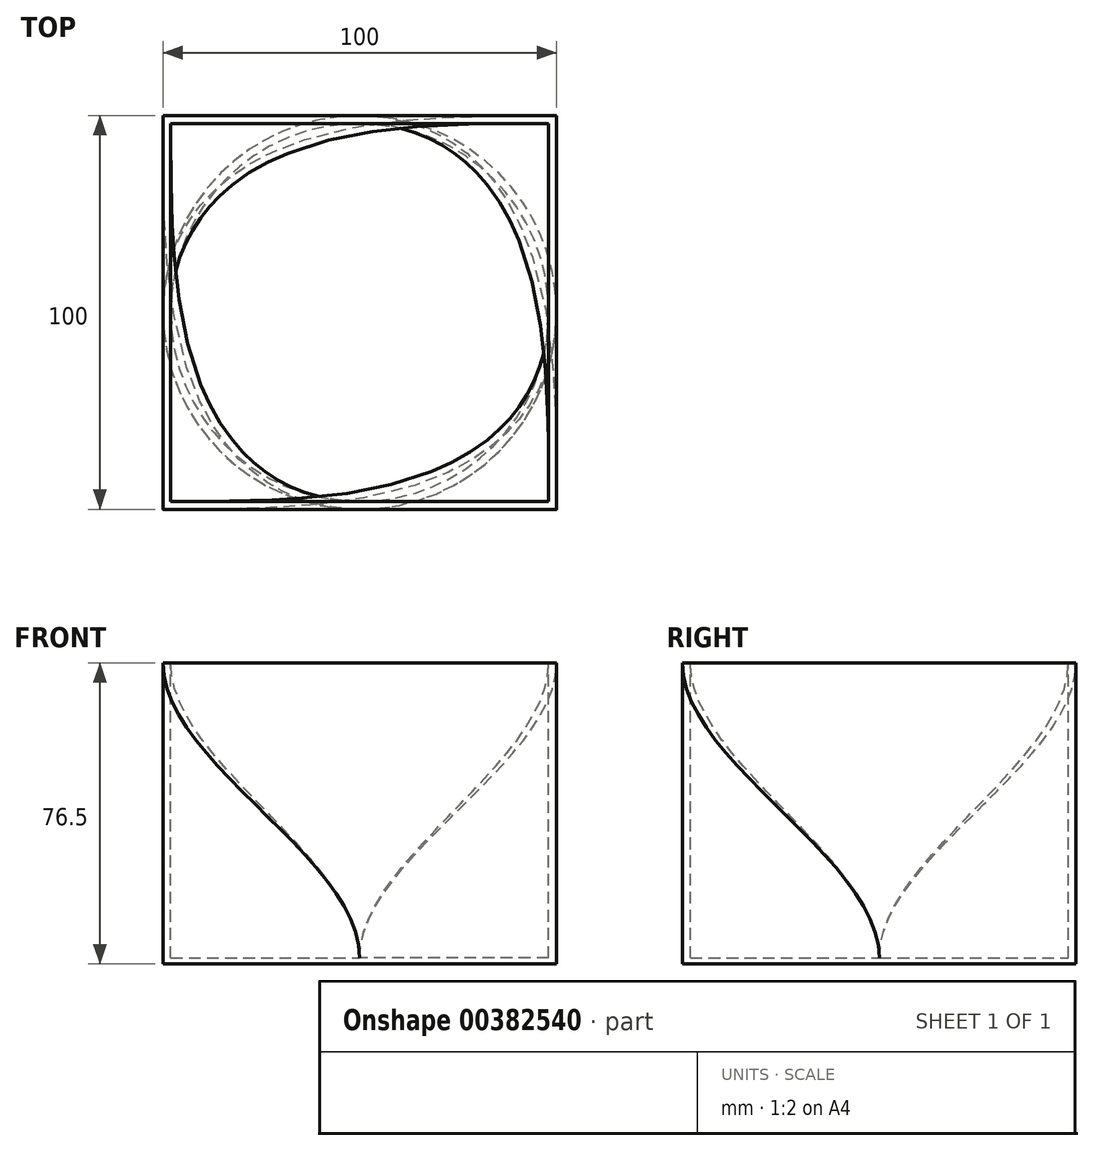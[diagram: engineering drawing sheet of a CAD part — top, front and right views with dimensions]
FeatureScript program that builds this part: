
annotation { "Feature Type Name" : "Feature", "Feature Type Description" : "" }
export const myFeature = defineFeature(function(context is Context, id is Id, definition is map)
    precondition{}
    {
        {
            var Q0;
            Q0=qCreatedBy(makeId("Top.planeOp"),FACE);
            var sketch = newSketch(context, id + "F0", { "sketchPlane" : qUnion([Q0])});
            skArc(sketch, "E0", {"start": v(0, 50) * mm, "mid": v(-35.36, 35.36) * mm, "end": v(-50, 0) * mm});
            skArc(sketch, "E1", {"start": v(50, 0) * mm, "mid": v(35.36, 35.36) * mm, "end": v(0, 50) * mm});
            skArc(sketch, "E2", {"start": v(0, -50) * mm, "mid": v(35.36, -35.36) * mm, "end": v(50, 0) * mm});
            skArc(sketch, "E3", {"start": v(-50, 0) * mm, "mid": v(-35.36, -35.36) * mm, "end": v(0, -50) * mm});
            skLineSegment(sketch, "E4", {"start": v(0, 57.4) * mm, "end": v(0, -65.17) * mm, "construction": true});
            skLineSegment(sketch, "E5", {"start": v(-56.88, 0) * mm, "end": v(63.58, 0) * mm, "construction": true});
            skSolve(sketch);
        }
        {
            var Q0;
            Q0=qCreatedBy(makeId("Top.planeOp"),FACE);
            cPlane(context, id + "F1", {"entities" : qUnion([Q0]), "cplaneType" : CPlaneType.OFFSET, "offset" : 75 * mm, "width" : 152.4 * mm, "height" : 152.4 * mm});
        }
        {
            var Q0;
            Q0=qCreatedBy(id+"F1.planeOp",FACE);
            var sketch = newSketch(context, id + "F2", { "sketchPlane" : qUnion([Q0])});
            skLineSegment(sketch, "E6.bottom", {"start": v(-50, 50) * mm, "end": v(50, 50) * mm});
            skLineSegment(sketch, "E6.top", {"start": v(-50, -50) * mm, "end": v(50, -50) * mm});
            skLineSegment(sketch, "E6.left", {"start": v(-50, 50) * mm, "end": v(-50, -50) * mm});
            skLineSegment(sketch, "E6.right", {"start": v(50, 50) * mm, "end": v(50, -50) * mm});
            skPoint(sketch, "E6.middle", {"position": v(0, 0) * mm});
            skSolve(sketch);
        }
        {
            var Q0;
            Q0=makeQuery(id+"F0.imprint","IMPRINT",FACE,{"disambiguationData":[TD([[makeQuery(id+"F0.imprint","IMPRINT",EDGE,{"derivedFrom":sQuery(id+"F0.wireOp",EDGE,"E0")}),1.0]])]});
            var Q1;
            Q1=makeQuery(id+"F2.imprint","IMPRINT",FACE,{"disambiguationData":[TD([[makeQuery(id+"F2.imprint","IMPRINT",EDGE,{"derivedFrom":sQuery(id+"F2.wireOp",EDGE,"E6.bottom")}),-1.0]])]});
            loft(context, id + "F3", {"startCondition" : LoftEndDerivativeType.NORMAL_TO_PROFILE, "startMagnitude" : 1, "endCondition" : LoftEndDerivativeType.NORMAL_TO_PROFILE, "endMagnitude" : 1, "sheetProfilesArray" : [{ "sheetProfileEntities" : qUnion([Q0]) }, { "sheetProfileEntities" : qUnion([Q1]) }]});
        }
        {
            var Q0;
            Q0=qCreatedBy(makeId("Top.planeOp"),FACE);
            var sketch = newSketch(context, id + "F4", { "sketchPlane" : qUnion([Q0])});
            skArc(sketch, "E7", {"start": v(0, 48) * mm, "mid": v(-33.94, 33.94) * mm, "end": v(-48, 0) * mm});
            skArc(sketch, "E8", {"start": v(48, 0) * mm, "mid": v(33.94, 33.94) * mm, "end": v(0, 48) * mm});
            skArc(sketch, "E9", {"start": v(0, -48) * mm, "mid": v(33.94, -33.94) * mm, "end": v(48, 0) * mm});
            skArc(sketch, "E10", {"start": v(-48, 0) * mm, "mid": v(-33.94, -33.94) * mm, "end": v(0, -48) * mm});
            skSolve(sketch);
        }
        {
            var Q0;
            Q0=makeQuery(id+"F2.imprint","IMPRINT",FACE,{"disambiguationData":[TD([[makeQuery(id+"F2.imprint","IMPRINT",EDGE,{"derivedFrom":sQuery(id+"F2.wireOp",EDGE,"E6.bottom")}),-1.0]])]});
            var sketch = newSketch(context, id + "F5", { "sketchPlane" : qUnion([Q0])});
            skLineSegment(sketch, "E11.bottom", {"start": v(-48, 48) * mm, "end": v(48, 48) * mm});
            skLineSegment(sketch, "E11.top", {"start": v(-48, -48) * mm, "end": v(48, -48) * mm});
            skLineSegment(sketch, "E11.left", {"start": v(-48, 48) * mm, "end": v(-48, -48) * mm});
            skLineSegment(sketch, "E11.right", {"start": v(48, 48) * mm, "end": v(48, -48) * mm});
            skPoint(sketch, "E11.middle", {"position": v(0, 0) * mm});
            skSolve(sketch);
        }
        {
            var Q0;
            Q0 = qSketchRegion(id + "F4", true);
            var Q1;
            Q1 = qSketchRegion(id + "F5", true);
            loft(context, id + "F6", {"operationType" : NewBodyOperationType.REMOVE, "startCondition" : LoftEndDerivativeType.NORMAL_TO_PROFILE, "startMagnitude" : 1, "endCondition" : LoftEndDerivativeType.NORMAL_TO_PROFILE, "endMagnitude" : 1, "sheetProfilesArray" : [{ "sheetProfileEntities" : qUnion([Q0]) }, { "sheetProfileEntities" : qUnion([Q1]) }]});
        }
        {
            var Q0;
            Q0=makeQuery(id+"F0.imprint","IMPRINT",FACE,{"disambiguationData":[TD([[makeQuery(id+"F0.imprint","IMPRINT",EDGE,{"derivedFrom":sQuery(id+"F0.wireOp",EDGE,"E0")}),1.0]])]});
            extrude(context, id + "F7", {"entities" : qUnion([Q0]), "operationType" : NewBodyOperationType.ADD, "oppositeDirection" : true, "depth" : 1.5 * mm});
        }
    });
